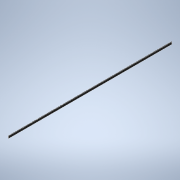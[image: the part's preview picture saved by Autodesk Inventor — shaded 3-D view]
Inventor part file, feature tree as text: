
AUTODESK INVENTOR PART (.ipt)
format: ipt  version: 2022.2 (Build 262287010, 287A)  size: 96,256 bytes
history: native  units: mm
features: extrude x1, sketch x1
ambient origin geometry x8: Origin, YZ Plane, XZ Plane, XY Plane, X Axis, Y Axis, Z Axis, Center Point
bodies: Volumenkörper1 (feature_tree)
feature tree (2):
  extrude  "Extrusion1"  Depth=450.0mm
  sketch  "Skizze1"  dims[d0=1.5mm d1=450.0mm d2=6.0mm d3=0.0mm]
